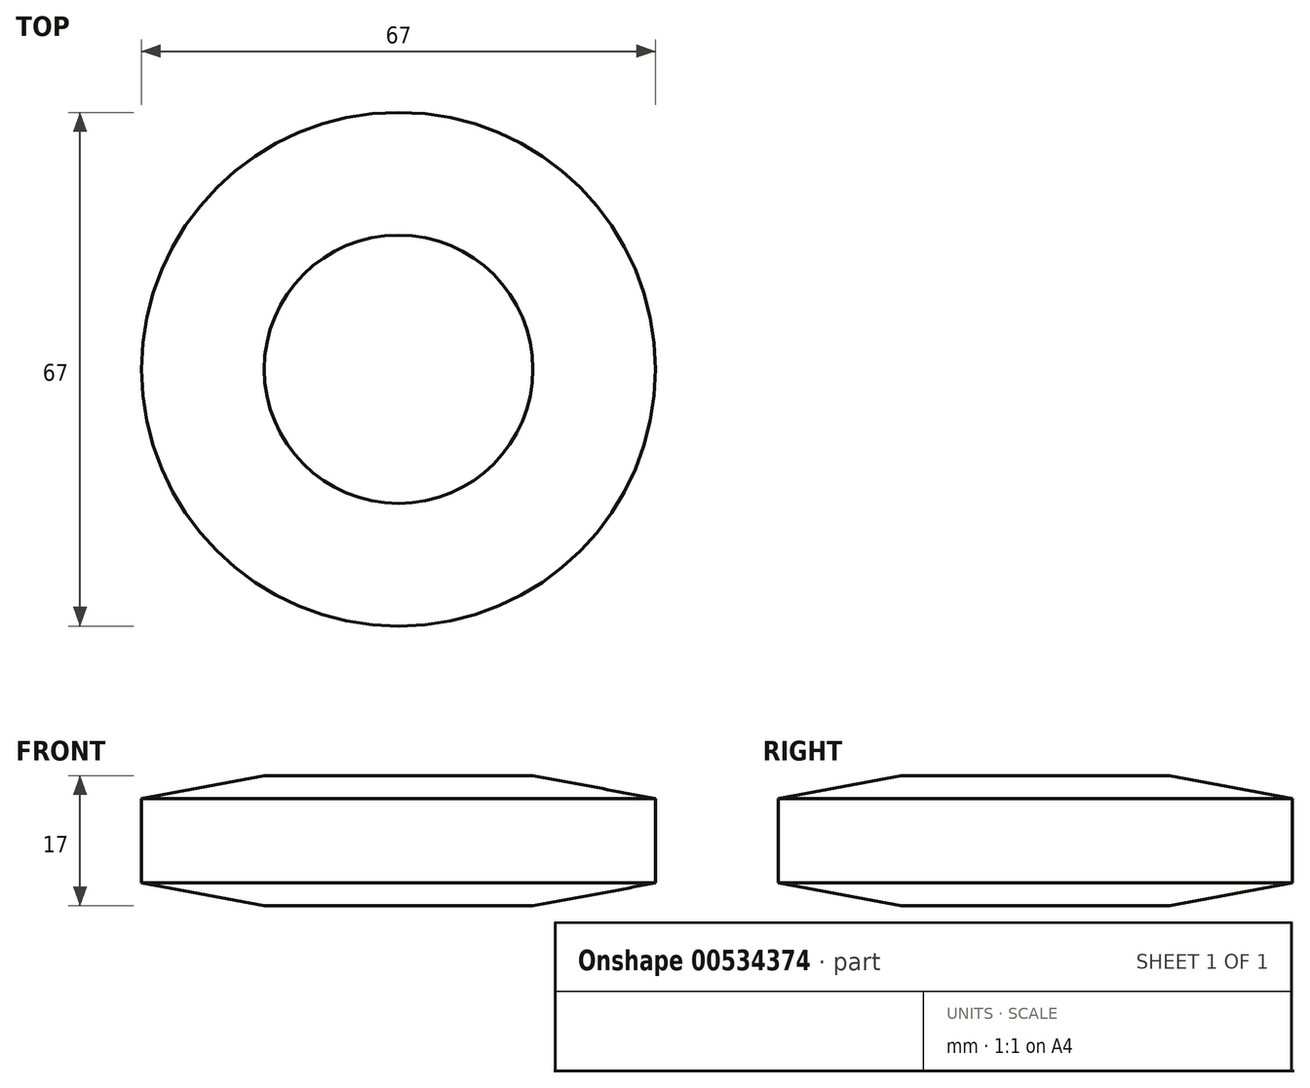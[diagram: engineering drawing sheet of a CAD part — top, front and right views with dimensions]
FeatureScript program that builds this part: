
annotation { "Feature Type Name" : "Feature", "Feature Type Description" : "" }
export const myFeature = defineFeature(function(context is Context, id is Id, definition is map)
    precondition{}
    {
        {
            var Q0;
            Q0=qCreatedBy(makeId("Top.planeOp"),FACE);
            var sketch = newSketch(context, id + "F0", { "sketchPlane" : qUnion([Q0])});
            skCircle(sketch, "E0", {"center": v(0, 0) * mm, "radius": 33.5 * mm});
            skSolve(sketch);
        }
        {
            var Q0;
            Q0 = qSketchRegion(id + "F0", true);
            extrude(context, id + "F1", {"entities" : qUnion([Q0]), "depth" : 17 * mm, "offsetDistance" : 25 * mm});
        }
        {
            var Q0;
            Q0=makeQuery(id+"F1.opExtrude","CAP_EDGE",EDGE,{"disambiguationData":[OSD([sQuery(id+"F0.wireOp",EDGE,"E0")])],"isStart":false});
            var Q1;
            Q1=makeQuery(id+"F1.opExtrude","CAP_EDGE",EDGE,{"disambiguationData":[OSD([sQuery(id+"F0.wireOp",EDGE,"E0")])],"isStart":true});
            chamfer(context, id + "F2", {"entities" : qUnion([Q0, Q1]), "chamferType" : ChamferType.TWO_OFFSETS, "width1" : 16 * mm, "oppositeDirection" : false, "width2" : 3 * mm, "tangentPropagation" : true});
        }
    });
